# Revit family: AFX-Twist-Led_Vanity
name_source: partatom
category: Lighting Fixtures
units: mm (PartAtom-declared; Revit-internal decimal feet)

## family parameters
Cut with Voids When Loaded = No
Host = Face
Light Source = Yes
Part Type = Normal
Room Calculation Point = No
Round Connector Dimension = Use Diameter
Shared = No

## types (2) — shared parameters
Apparent Load = 0 VA
Assembly Code = D5020200
Color Filter = 16777215
Colour Rendering Index = 80
Default Elevation = 48"
Depth = 4"
Dimming Lamp Color Temperature Shift = <None>
Frame Finish = AFX - Black Steel
Height = 3 1/2"
Housing Finish = AFX - Black Steel
Keynote = 12500
Led Finish = AFX - White Acrylic
Manufacturer = AFX Inc
Power Factor = 1
Product Documentation Link = https://www.afxinc.com
Revit File Built By = https://servex-us.com
Supports Finish = AFX - Black Steel
Sustainability = https://lamprecycle.org
Tilt Angle = 90.00°
Type Comments = Twist
URL = https://www.afxinc.com
Voltage = 120 V
Wattage Comments = 9

## per-type parameters (varying)
| type | Description | Emit from Line Length | Length | Photometric Web File |
| TWTV2405L30D1BK | Led Vanity - 24"L x 3 1/2"H x 4"D | 24" | 24" | TWTV2405L30D1xx_IES.IES |
| TWTV3605L30D1BK | Led Vanity - 35 3/4"L x 3 1/2"H x 4"D | 35" | 35 3/4" | TWTV3605L30D1xx_IES.IES |

note: column(s) folded — value = type name in every type: Model

## geometry (parser evidence)
native form markers: Sweep x4
no freeform markers — native parametric forms only
